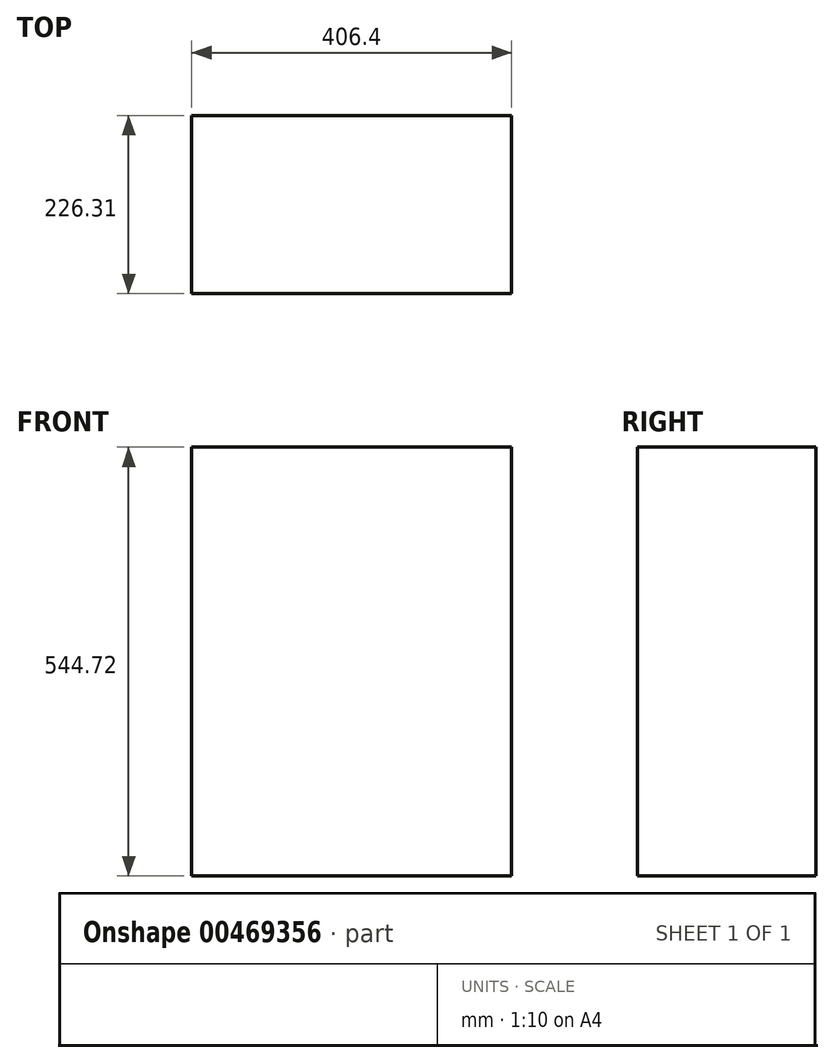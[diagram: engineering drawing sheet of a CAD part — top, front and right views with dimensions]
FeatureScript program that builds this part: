
annotation { "Feature Type Name" : "Feature", "Feature Type Description" : "" }
export const myFeature = defineFeature(function(context is Context, id is Id, definition is map)
    precondition{}
    {
        {
            var Q0;
            Q0=qCreatedBy(makeId("Front.planeOp"),FACE);
            var sketch = newSketch(context, id + "F0", { "sketchPlane" : qUnion([Q0])});
            skLineSegment(sketch, "E0.bottom", {"start": v(-308.33, 231.16) * mm, "end": v(98.07, 231.16) * mm});
            skLineSegment(sketch, "E0.top", {"start": v(-308.33, -313.56) * mm, "end": v(98.07, -313.56) * mm});
            skLineSegment(sketch, "E0.left", {"start": v(-308.33, 231.16) * mm, "end": v(-308.33, -313.56) * mm});
            skLineSegment(sketch, "E0.right", {"start": v(98.07, 231.16) * mm, "end": v(98.07, -313.56) * mm});
            skSolve(sketch);
        }
        {
            var Q0;
            Q0=makeQuery(id+"F0.imprint","IMPRINT",FACE,{"disambiguationData":[TD([[makeQuery(id+"F0.imprint","IMPRINT",EDGE,{"derivedFrom":sQuery(id+"F0.wireOp",EDGE,"E0.bottom")}),-1.0]])]});
            var sketch = newSketch(context, id + "F1", { "sketchPlane" : qUnion([Q0])});
            skSolve(sketch);
        }
        {
            var Q0;
            Q0=makeQuery(id+"F0.imprint","IMPRINT",FACE,{"disambiguationData":[TD([[makeQuery(id+"F0.imprint","IMPRINT",EDGE,{"derivedFrom":sQuery(id+"F0.wireOp",EDGE,"E0.bottom")}),-1.0]])]});
            extrude(context, id + "F2", {"entities" : qUnion([Q0]), "depth" : 179.83 * mm});
        }
        {
            var Q0;
            Q0=makeQuery(id+"F2.opExtrude","CAP_FACE",FACE,{"disambiguationData":[OSD([sQuery(id+"F0.wireOp",EDGE,"E0.bottom"),sQuery(id+"F0.wireOp",EDGE,"E0.top"),sQuery(id+"F0.wireOp",EDGE,"E0.left"),sQuery(id+"F0.wireOp",EDGE,"E0.right")])],"isStart":false});
            var sketch = newSketch(context, id + "F3", { "sketchPlane" : qUnion([Q0])});
            skSolve(sketch);
        }
        {
            var Q0;
            Q0 = qSketchRegion(id + "F3", true);
            var Q1;
            Q1=makeQuery(id+"F3.imprint","IMPRINT",FACE,{"disambiguationData":[TD([[makeQuery(id+"F3.imprint","IMPRINT",EDGE,{"derivedFrom":makeQuery(id+"F2.opExtrude","CAP_EDGE",EDGE,{"disambiguationData":[OSD([sQuery(id+"F0.wireOp",EDGE,"E0.bottom")])],"isStart":false})}),-1.0]])]});
            extrude(context, id + "F4", {"entities" : qUnion([Q0, Q1]), "operationType" : NewBodyOperationType.REMOVE, "oppositeDirection" : true, "depth" : 171.7 * mm});
        }
        {
            var Q0;
            Q0=makeQuery(id+"F4.boolean.opBoolean","COPY",FACE,{"derivedFrom":makeQuery(id+"F4.opExtrude","CAP_FACE",FACE,{"disambiguationData":[OSD([sQuery(id+"F0.wireOp",EDGE,"E0.bottom"),sQuery(id+"F0.wireOp",EDGE,"E0.top"),sQuery(id+"F0.wireOp",EDGE,"E0.left"),sQuery(id+"F0.wireOp",EDGE,"E0.right")])],"isStart":false})});
            var sketch = newSketch(context, id + "F5", { "sketchPlane" : qUnion([Q0])});
            skSolve(sketch);
        }
        {
            var Q0;
            Q0=makeQuery(id+"F5.imprint","IMPRINT",FACE,{"disambiguationData":[TD([[makeQuery(id+"F5.imprint","IMPRINT",EDGE,{"derivedFrom":makeQuery(id+"F4.boolean.opBoolean","COPY",EDGE,{"derivedFrom":makeQuery(id+"F4.opExtrude","CAP_EDGE",EDGE,{"disambiguationData":[OSD([sQuery(id+"F0.wireOp",EDGE,"E0.bottom")])],"isStart":false})})}),-1.0]])]});
            var sketch = newSketch(context, id + "F6", { "sketchPlane" : qUnion([Q0])});
            skSolve(sketch);
        }
        {
            var Q0;
            Q0 = qSketchRegion(id + "F6", true);
            var Q1;
            Q1=makeQuery(id+"F6.imprint","IMPRINT",FACE,{"disambiguationData":[TD([[makeQuery(id+"F6.imprint","IMPRINT",EDGE,{"derivedFrom":makeQuery(id+"F5.imprint","IMPRINT",EDGE,{"derivedFrom":makeQuery(id+"F4.boolean.opBoolean","COPY",EDGE,{"derivedFrom":makeQuery(id+"F4.opExtrude","CAP_EDGE",EDGE,{"disambiguationData":[OSD([sQuery(id+"F0.wireOp",EDGE,"E0.bottom")])],"isStart":false})})})}),-1.0]])]});
            var Q2;
            Q2=makeQuery(id+"F4.boolean.opBoolean","COPY",FACE,{"derivedFrom":makeQuery(id+"F4.opExtrude","CAP_FACE",FACE,{"disambiguationData":[OSD([sQuery(id+"F0.wireOp",EDGE,"E0.bottom"),sQuery(id+"F0.wireOp",EDGE,"E0.top"),sQuery(id+"F0.wireOp",EDGE,"E0.left"),sQuery(id+"F0.wireOp",EDGE,"E0.right")])],"isStart":false})});
            var Q3;
            Q3=makeQuery(id+"F1.imprint","IMPRINT",FACE,{"disambiguationData":[TD([[makeQuery(id+"F1.imprint","IMPRINT",EDGE,{"derivedFrom":makeQuery(id+"F0.imprint","IMPRINT",EDGE,{"derivedFrom":sQuery(id+"F0.wireOp",EDGE,"E0.bottom")})}),-1.0]])]});
            var Q4;
            Q4=makeQuery(id+"F2.opExtrude","CAP_FACE",FACE,{"disambiguationData":[OSD([sQuery(id+"F0.wireOp",EDGE,"E0.bottom"),sQuery(id+"F0.wireOp",EDGE,"E0.top"),sQuery(id+"F0.wireOp",EDGE,"E0.left"),sQuery(id+"F0.wireOp",EDGE,"E0.right")])],"isStart":true});
            extrude(context, id + "F7", {"entities" : qUnion([Q0, Q1, Q2, Q3, Q4]), "operationType" : NewBodyOperationType.ADD, "depth" : 218.2 * mm});
        }
    });
